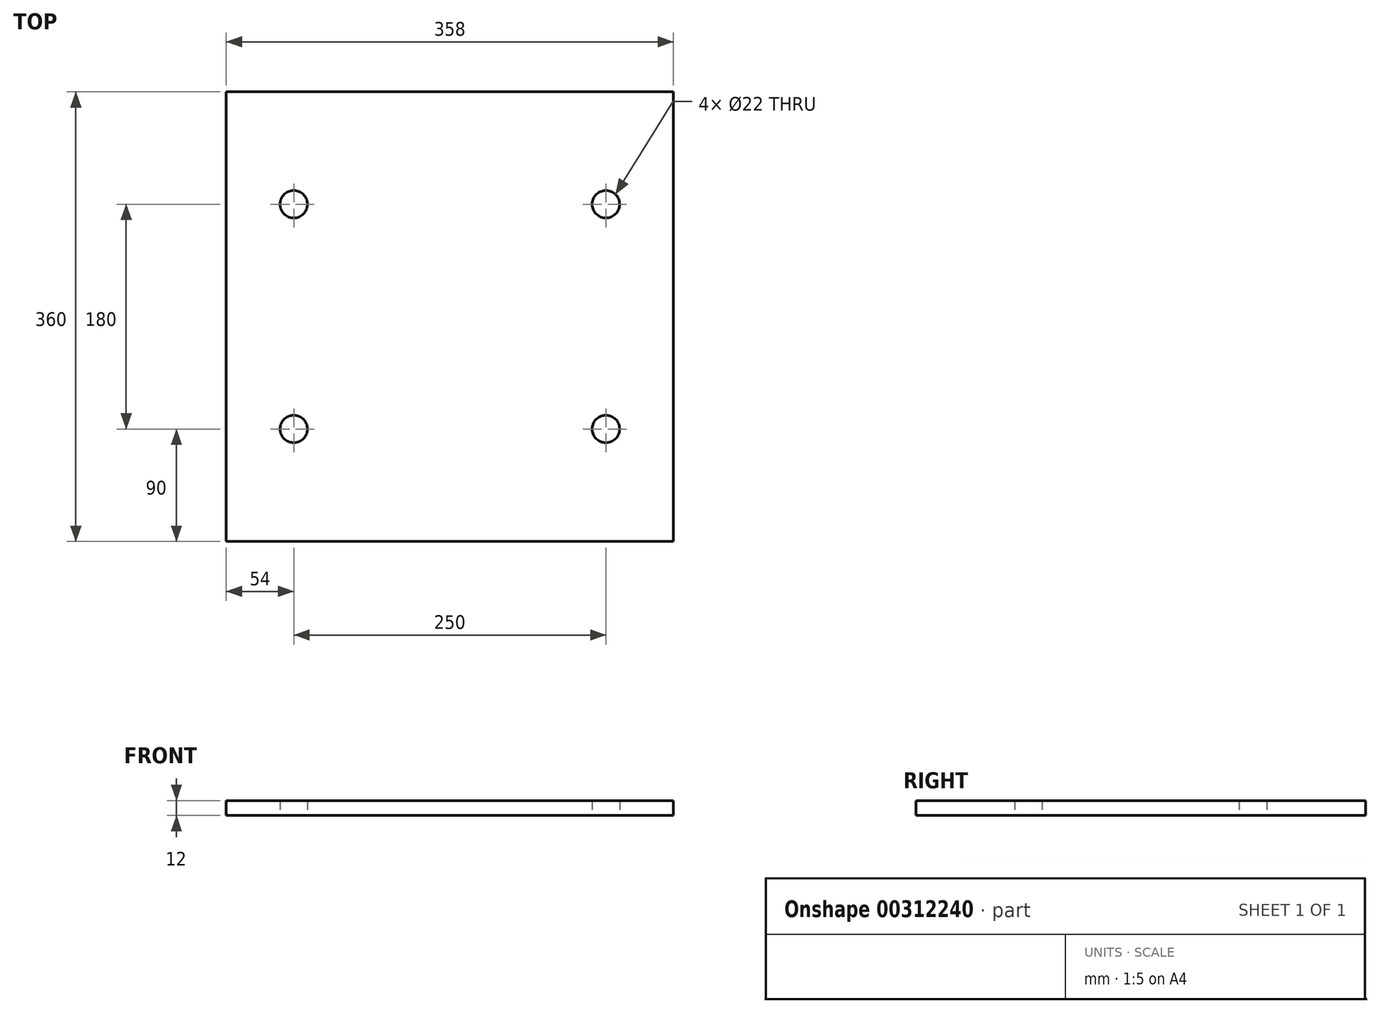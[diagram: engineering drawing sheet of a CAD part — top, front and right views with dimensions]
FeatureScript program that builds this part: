
annotation { "Feature Type Name" : "Feature", "Feature Type Description" : "" }
export const myFeature = defineFeature(function(context is Context, id is Id, definition is map)
    precondition{}
    {
        {
            var Q0;
            Q0=qCreatedBy(makeId("Top.planeOp"),FACE);
            var sketch = newSketch(context, id + "F0", { "sketchPlane" : qUnion([Q0])});
            skLineSegment(sketch, "E0", {"start": v(-179, 180) * mm, "end": v(179, 180) * mm});
            skLineSegment(sketch, "E1", {"start": v(179, 180) * mm, "end": v(179, -180) * mm});
            skLineSegment(sketch, "E2", {"start": v(179, -180) * mm, "end": v(-179, -180) * mm});
            skLineSegment(sketch, "E3", {"start": v(-179, -180) * mm, "end": v(-179, 180) * mm});
            skCircle(sketch, "E4", {"center": v(125, 90) * mm, "radius": 11 * mm});
            skCircle(sketch, "E5", {"center": v(125, -90) * mm, "radius": 11 * mm});
            skCircle(sketch, "E6", {"center": v(-125, -90) * mm, "radius": 11 * mm});
            skCircle(sketch, "E7", {"center": v(-125, 90) * mm, "radius": 11 * mm});
            skSolve(sketch);
        }
        {
            var Q0;
            Q0 = qSketchRegion(id + "F0", true);
            extrude(context, id + "F1", {"entities" : qUnion([Q0]), "depth" : 12 * mm, "offsetDistance" : 25 * mm});
        }
    });
